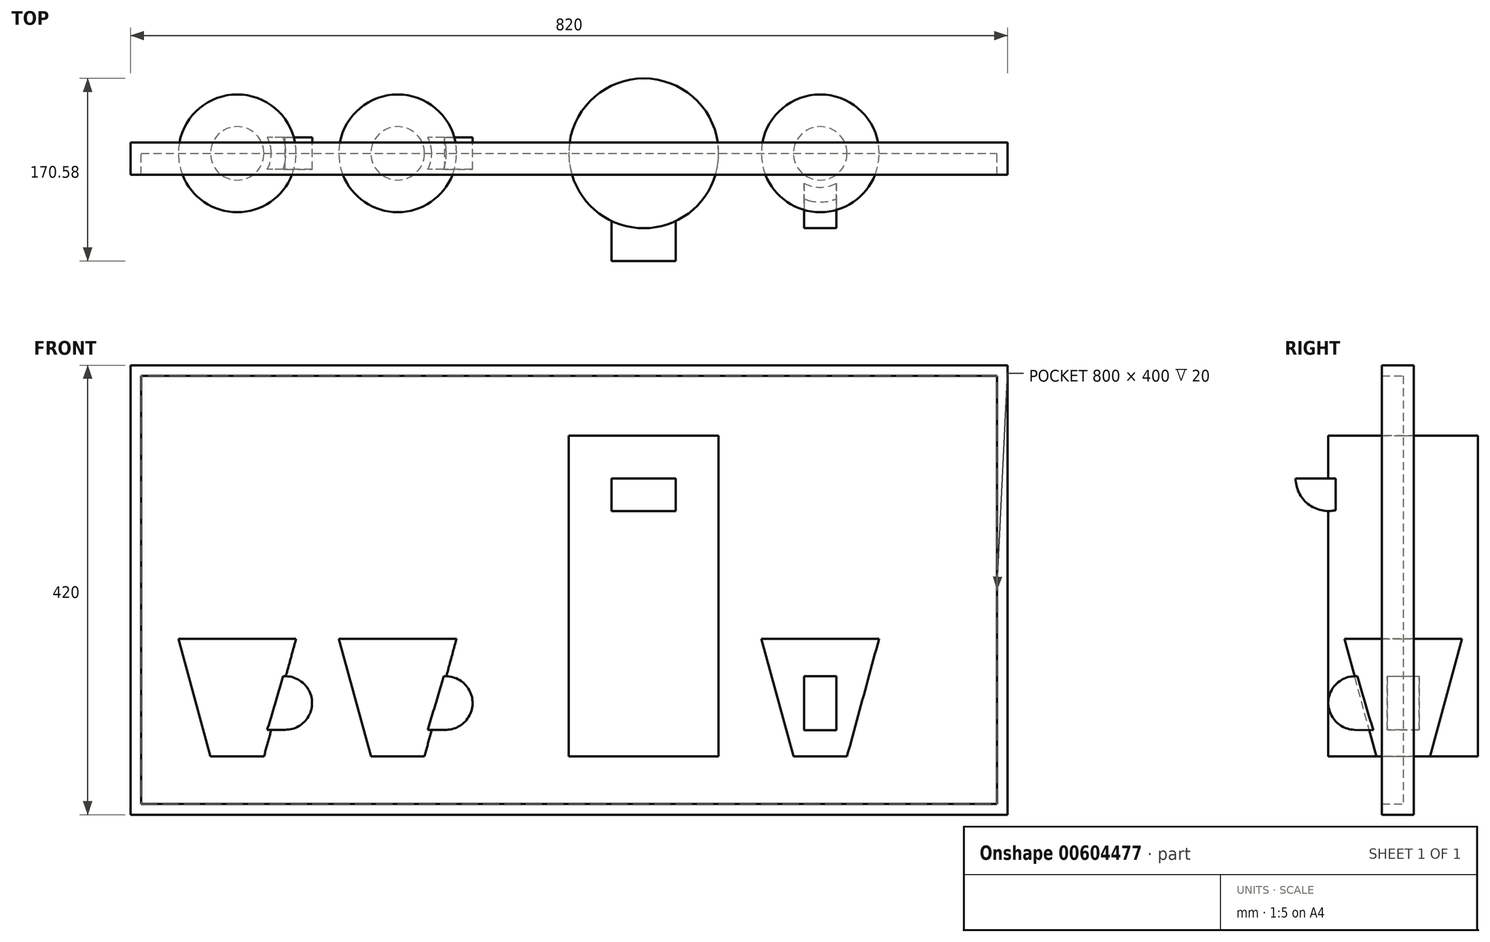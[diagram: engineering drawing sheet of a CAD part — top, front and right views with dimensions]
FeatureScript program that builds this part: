
annotation { "Feature Type Name" : "Feature", "Feature Type Description" : "" }
export const myFeature = defineFeature(function(context is Context, id is Id, definition is map)
    precondition{}
    {
        {
            var Q0;
            Q0=qCreatedBy(makeId("Top.planeOp"),FACE);
            cPlane(context, id + "F0", {"entities" : qUnion([Q0]), "cplaneType" : CPlaneType.OFFSET, "offset" : 110 * mm, "width" : 150 * mm, "height" : 150 * mm});
        }
        {
            var Q0;
            Q0=qCreatedBy(makeId("Top.planeOp"),FACE);
            var sketch = newSketch(context, id + "F1", { "sketchPlane" : qUnion([Q0])});
            skCircle(sketch, "E0", {"center": v(70, 0) * mm, "radius": 70 * mm});
            skSolve(sketch);
        }
        {
            var Q0;
            Q0 = qSketchRegion(id + "F1", true);
            var Q1;
            Q1 = qSketchRegion(id + "F3", true);
            extrude(context, id + "F2", {"entities" : qUnion([Q0, Q1]), "depth" : 300 * mm, "offsetDistance" : 25 * mm});
        }
        {
            var Q0;
            Q0=qCreatedBy(makeId("Top.planeOp"),FACE);
            var sketch = newSketch(context, id + "F3", { "sketchPlane" : qUnion([Q0])});
            skCircle(sketch, "E1", {"center": v(235, 0) * mm, "radius": 25 * mm});
            skSolve(sketch);
        }
        {
            var Q0;
            Q0=qCreatedBy(id+"F0.planeOp",FACE);
            var sketch = newSketch(context, id + "F4", { "sketchPlane" : qUnion([Q0])});
            skCircle(sketch, "E2", {"center": v(235, 0) * mm, "radius": 55 * mm});
            skSolve(sketch);
        }
        {
            var Q0;
            Q0 = qSketchRegion(id + "F3", true);
            var Q1;
            Q1 = qSketchRegion(id + "F4", true);
            loft(context, id + "F5", {"sheetProfilesArray" : [{ "sheetProfileEntities" : qUnion([Q0]) }, { "sheetProfileEntities" : qUnion([Q1]) }]});
        }
        {
            var Q0;
            Q0=qCreatedBy(makeId("Top.planeOp"),FACE);
            var sketch = newSketch(context, id + "F6", { "sketchPlane" : qUnion([Q0])});
            skCircle(sketch, "E3", {"center": v(-160, 0) * mm, "radius": 25 * mm});
            skSolve(sketch);
        }
        {
            var Q0;
            Q0=qCreatedBy(id+"F0.planeOp",FACE);
            var sketch = newSketch(context, id + "F7", { "sketchPlane" : qUnion([Q0])});
            skCircle(sketch, "E4", {"center": v(-160, 0) * mm, "radius": 55 * mm});
            skSolve(sketch);
        }
        {
            var Q0;
            Q0 = qSketchRegion(id + "F6", true);
            var Q1;
            Q1 = qSketchRegion(id + "F7", true);
            loft(context, id + "F8", {"sheetProfilesArray" : [{ "sheetProfileEntities" : qUnion([Q0]) }, { "sheetProfileEntities" : qUnion([Q1]) }]});
        }
        {
            var Q0;
            Q0=qCreatedBy(makeId("Top.planeOp"),FACE);
            var sketch = newSketch(context, id + "F9", { "sketchPlane" : qUnion([Q0])});
            skCircle(sketch, "E5", {"center": v(-310, 0) * mm, "radius": 25 * mm});
            skSolve(sketch);
        }
        {
            var Q0;
            Q0=qCreatedBy(id+"F0.planeOp",FACE);
            var sketch = newSketch(context, id + "F10", { "sketchPlane" : qUnion([Q0])});
            skCircle(sketch, "E6", {"center": v(-310, 0) * mm, "radius": 55 * mm});
            skSolve(sketch);
        }
        {
            var Q0;
            Q0 = qSketchRegion(id + "F9", true);
            var Q1;
            Q1 = qSketchRegion(id + "F10", true);
            loft(context, id + "F11", {"sheetProfilesArray" : [{ "sheetProfileEntities" : qUnion([Q0]) }, { "sheetProfileEntities" : qUnion([Q1]) }]});
        }
        {
            var Q0;
            Q0=qCreatedBy(makeId("Right.planeOp"),FACE);
            cPlane(context, id + "F12", {"entities" : qUnion([Q0]), "cplaneType" : CPlaneType.OFFSET, "offset" : 70 * mm, "width" : 150 * mm, "height" : 150 * mm});
        }
        {
            var Q0;
            Q0=qCreatedBy(id+"F12.planeOp",FACE);
            var sketch = newSketch(context, id + "F13", { "sketchPlane" : qUnion([Q0])});
            skArc(sketch, "E7", {"start": v(-100.58, 259.93) * mm, "mid": v(-70, 229.42) * mm, "end": v(-39.42, 259.93) * mm});
            skLineSegment(sketch, "E8", {"start": v(-39.42, 259.93) * mm, "end": v(-100.58, 259.93) * mm});
            skSolve(sketch);
        }
        {
            var Q0;
            Q0 = qSketchRegion(id + "F13", true);
            extrude(context, id + "F14", {"entities" : qUnion([Q0]), "operationType" : NewBodyOperationType.ADD, "endBound" : BoundingType.SYMMETRIC, "depth" : 60 * mm, "offsetDistance" : 25 * mm});
        }
        {
            var Q0;
            Q0=qCreatedBy(makeId("Right.planeOp"),FACE);
            cPlane(context, id + "F15", {"entities" : qUnion([Q0]), "cplaneType" : CPlaneType.OFFSET, "offset" : 235 * mm, "width" : 150 * mm, "height" : 150 * mm});
        }
        {
            var Q0;
            Q0=qCreatedBy(id+"F15.planeOp",FACE);
            var sketch = newSketch(context, id + "F16", { "sketchPlane" : qUnion([Q0])});
            skArc(sketch, "E9", {"start": v(-44.02, 74.98) * mm, "mid": v(-69.99, 50.74) * mm, "end": v(-45.51, 25) * mm});
            skLineSegment(sketch, "E10", {"start": v(-45.51, 25) * mm, "end": v(-13.64, 24.35) * mm});
            skLineSegment(sketch, "E11", {"start": v(-13.64, 24.35) * mm, "end": v(-13.64, 73.8) * mm});
            skLineSegment(sketch, "E12", {"start": v(-13.64, 73.8) * mm, "end": v(-44.02, 74.98) * mm});
            skSolve(sketch);
        }
        {
            var Q0;
            Q0 = qSketchRegion(id + "F16", true);
            extrude(context, id + "F17", {"entities" : qUnion([Q0]), "operationType" : NewBodyOperationType.ADD, "endBound" : BoundingType.SYMMETRIC, "depth" : 30 * mm, "offsetDistance" : 25 * mm});
        }
        {
            var Q0;
            Q0=qCreatedBy(makeId("Front.planeOp"),FACE);
            var sketch = newSketch(context, id + "F18", { "sketchPlane" : qUnion([Q0])});
            skArc(sketch, "E13", {"start": v(-115.89, 25.02) * mm, "mid": v(-90, 49.5) * mm, "end": v(-114.88, 75) * mm});
            skLineSegment(sketch, "E14", {"start": v(-115.89, 25.02) * mm, "end": v(-153.4, 25.02) * mm});
            skLineSegment(sketch, "E15", {"start": v(-153.4, 25.02) * mm, "end": v(-153.4, 75.18) * mm});
            skLineSegment(sketch, "E16", {"start": v(-153.4, 75.18) * mm, "end": v(-114.88, 75) * mm});
            skSolve(sketch);
        }
        {
            var Q0;
            Q0 = qSketchRegion(id + "F18", true);
            extrude(context, id + "F19", {"entities" : qUnion([Q0]), "operationType" : NewBodyOperationType.ADD, "endBound" : BoundingType.SYMMETRIC, "depth" : 30 * mm, "offsetDistance" : 25 * mm});
        }
        {
            var Q0;
            Q0=qCreatedBy(makeId("Front.planeOp"),FACE);
            var sketch = newSketch(context, id + "F20", { "sketchPlane" : qUnion([Q0])});
            skArc(sketch, "E17", {"start": v(-265.26, 25) * mm, "mid": v(-240, 50.18) * mm, "end": v(-265.62, 75) * mm});
            skLineSegment(sketch, "E18", {"start": v(-264.74, 25) * mm, "end": v(-307.4, 25) * mm});
            skLineSegment(sketch, "E19", {"start": v(-307.4, 25) * mm, "end": v(-307.4, 73.96) * mm});
            skLineSegment(sketch, "E20", {"start": v(-307.4, 73.96) * mm, "end": v(-265.62, 75) * mm});
            skSolve(sketch);
        }
        {
            var Q0;
            Q0 = qSketchRegion(id + "F20", true);
            extrude(context, id + "F21", {"entities" : qUnion([Q0]), "operationType" : NewBodyOperationType.ADD, "endBound" : BoundingType.SYMMETRIC, "depth" : 30 * mm, "offsetDistance" : 25 * mm});
        }
        {
            var Q0;
            Q0=qCreatedBy(makeId("Front.planeOp"),FACE);
            var sketch = newSketch(context, id + "F22", { "sketchPlane" : qUnion([Q0])});
            skLineSegment(sketch, "E21.bottom", {"start": v(-399.84, 355.64) * mm, "end": v(400.16, 355.64) * mm});
            skLineSegment(sketch, "E21.top", {"start": v(-399.84, -44.36) * mm, "end": v(400.16, -44.36) * mm});
            skLineSegment(sketch, "E21.left", {"start": v(-399.84, 355.64) * mm, "end": v(-399.84, -44.36) * mm});
            skLineSegment(sketch, "E21.right", {"start": v(400.16, 355.64) * mm, "end": v(400.16, -44.36) * mm});
            skSolve(sketch);
        }
        {
            var Q0;
            Q0 = qSketchRegion(id + "F22", true);
            extrude(context, id + "F23", {"entities" : qUnion([Q0]), "depth" : 20 * mm, "offsetDistance" : 25 * mm});
        }
        {
            var Q0;
            Q0=makeQuery(id+"F23.opExtrude","CAP_FACE",FACE,{"disambiguationData":[OSD([sQuery(id+"F22.wireOp",EDGE,"E21.bottom"),sQuery(id+"F22.wireOp",EDGE,"E21.top"),sQuery(id+"F22.wireOp",EDGE,"E21.left"),sQuery(id+"F22.wireOp",EDGE,"E21.right")])],"isStart":false});
            shell(context, id + "F24", {"entities" : qUnion([Q0]), "thickness" : 10 * mm, "oppositeDirection" : true});
        }
    });
